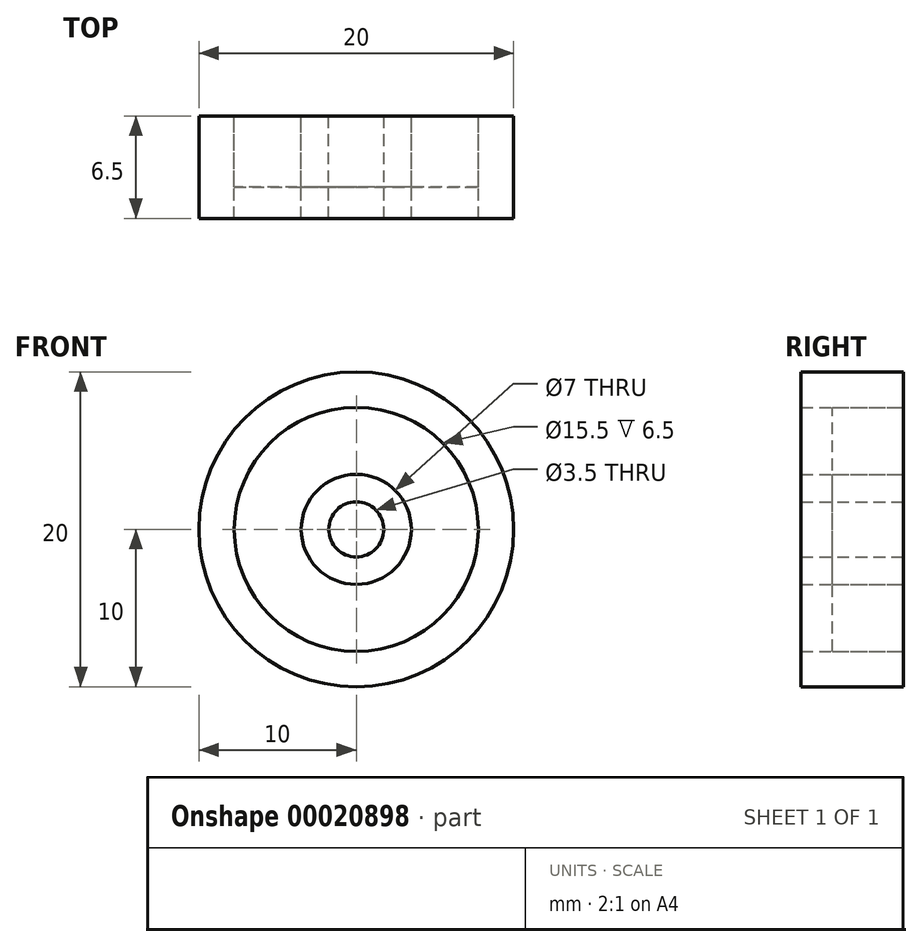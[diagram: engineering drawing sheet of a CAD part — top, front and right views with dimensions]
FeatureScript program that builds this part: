
annotation { "Feature Type Name" : "Feature", "Feature Type Description" : "" }
export const myFeature = defineFeature(function(context is Context, id is Id, definition is map)
    precondition{}
    {
        {
            var Q0;
            Q0=qCreatedBy(makeId("Front.planeOp"),FACE);
            var sketch = newSketch(context, id + "F0", { "sketchPlane" : qUnion([Q0])});
            skCircle(sketch, "E0", {"center": v(0, 0) * mm, "radius": 10 * mm});
            skCircle(sketch, "E1", {"center": v(0, 0) * mm, "radius": 7.75 * mm});
            skCircle(sketch, "E2", {"center": v(0, 0) * mm, "radius": 3.5 * mm});
            skCircle(sketch, "E3", {"center": v(0, 0) * mm, "radius": 1.75 * mm});
            skSolve(sketch);
        }
        {
            var Q0;
            Q0=makeQuery(id+"F0.imprint","IMPRINT",FACE,{"disambiguationData":[TD([[makeQuery(id+"F0.imprint","IMPRINT",EDGE,{"derivedFrom":sQuery(id+"F0.wireOp",EDGE,"E0")}),1.0]])]});
            var Q1;
            Q1=makeQuery(id+"F0.imprint","IMPRINT",FACE,{"disambiguationData":[TD([[makeQuery(id+"F0.imprint","IMPRINT",EDGE,{"derivedFrom":sQuery(id+"F0.wireOp",EDGE,"E2")}),1.0]])]});
            extrude(context, id + "F1", {"entities" : qUnion([Q0, Q1]), "depth" : 6.5 * mm});
        }
        {
            var Q0;
            Q0=makeQuery(id+"F0.imprint","IMPRINT",FACE,{"disambiguationData":[TD([[makeQuery(id+"F0.imprint","IMPRINT",EDGE,{"derivedFrom":sQuery(id+"F0.wireOp",EDGE,"E1")}),1.0]])]});
            extrude(context, id + "F2", {"entities" : qUnion([Q0]), "depth" : 4.5 * mm});
        }
    });
